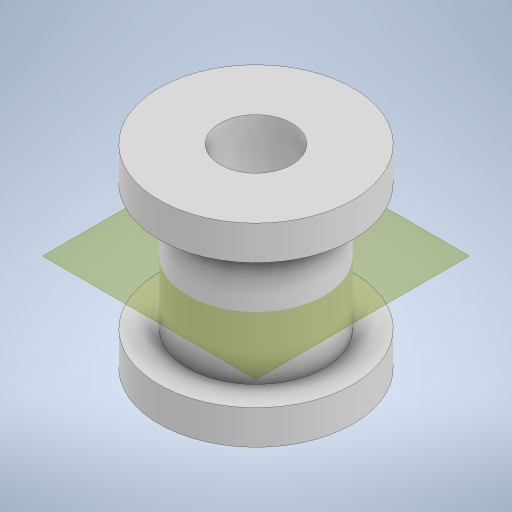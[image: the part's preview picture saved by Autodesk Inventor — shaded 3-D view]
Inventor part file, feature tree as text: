
AUTODESK INVENTOR PART (.ipt)
format: ipt  version: 2023 (Build 270158000, 158)  size: 248,832 bytes
history: native  units: mm
features: extrude x2, plane x2, sketch x2, mirror x1
ambient origin geometry x8: Origin, YZ Plane, XZ Plane, XY Plane, X Axis, Y Axis, Z Axis, Center Point
bodies: Solid1 (feature_tree)
feature tree (7):
  extrude  "Extrusion1"  Depth=12.0mm
  extrude  "Extrusion2"  Depth=17.0mm
  plane  "Work Plane1"
  mirror  "Mirror1"
  sketch  "Sketch1"  dims[d0=6.3mm d2=12.0mm]
  sketch  "Sketch2"  dims[d3=14.0mm d4=0.0mm d5=17.0mm d6=3.0mm d7=0.0mm]
  plane  "Work Plane2"
